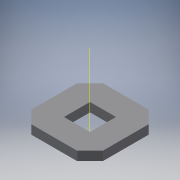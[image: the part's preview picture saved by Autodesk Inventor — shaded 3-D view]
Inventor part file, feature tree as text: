
AUTODESK INVENTOR PART (.ipt)
format: ipt  version: 2017 SP1 (Build 210196100, 196)  size: 1,112,576 bytes
history: native  units: in
note: dims shown in document units (in); Inventor stores cm internally (conversion verified against a paired STEP export)
features: other x10, extrude x2, pattern_linear x1, imported_body x1
ambient origin geometry x8: Origin, YZ Plane, XZ Plane, XY Plane, X Axis, Y Axis, Z Axis, Center Point
bodies: Body1 (feature_tree)
feature tree (14):
  other  "Diamond-Pattern"
  other  "Plate"
  extrude  "length cut"  TaperAngle=0.0deg  [1 undecoded]
  extrude  "width cut"  TaperAngle=0.0deg  [1 undecoded]
  other  "constraint axis"
  pattern_linear  "constraint axes"  Spacing1=0.5in  [1 undecoded]
  other  "front plane"
  other  "right plane"
  imported_body  "Base1"
  other  "length profile"
  other  "width profile"
  other  "Work Point1"
  other  "back plane"
  other  "left plane"
note: 3 required parameter values undecoded (feature->parameter linkage not recoverable at this tier; creation-order binding heuristic only, values carry confidence <= 0.55)
